# Revit family: Doorset_Porte palière blindée destinée au projet de réhabilitation BELLECOUR_ASSA ABLOY FR_Hardware 3D-05
name_source: partatom
category: Doors
revit_build: Autodesk Revit 2015 (Build: 20160512_0715(x64)
units: mm (PartAtom-declared; Revit-internal decimal feet)

## types (1)
- 914x2198 mm (900 x 2200mm)
    Architectural Hardware = 1x Ensemble béquillage SCULT_Architectural hardware_Vachette [AN. 204367 4]
    Assembly Code = B2030
    BIMobject Brand = ASSA ABLOY FR
    BIMobject Product Family = Exterior Door Solutions
    BIMobject Product Group = Security doors and fittings
    BIMobject Product Page = https://www.bimobject.com
    BIMobject Unique ref = ED-ML-MC-FR16
    Clear Width = 852 mm  [stored 2.79528 ft]
    Description = La porte anti-effraction certifiée  A2P BP1
    Edition number = 1
    Frame Height = 2200 mm
    Frame Material = Metal - Assa Abloy - Steel
    Frame Width = 900 mm  [stored 2.95276 ft]
    Function = Exterior
    Handle Height = 1100 mm
    Handle Position = 81 mm  [stored 0.265748 ft]
    Hardware Set = ED-ML-MC-FR16
    Height = 2200 mm
    IFC classification = Door
    Identity and Access Solutions = 1x Serrure 5000 SPN1 T204- D_Identity and Access Solutions_Vachette [AN. 841900 4]
    Keynote = 08100
    Lock Cases = 1x Cylindre GEMMCODE_Mechanical locks_Fichet [AN. 73960050]
    Manufacturer = ASSA ABLOY
    Maximum Door Height = 2325 mm
    Maximum Door Width = 1050 mm
    Minimum Door Height = 1952 mm  [stored 6.4042 ft]
    Minimum Door Width = 650 mm  [stored 2.13255 ft]
    Model = Doorset_Porte palière blindée destinée au projet de réhabilitation BELLECOUR_ASSA ABLOY FR_Hardware 3D
    Name = Porte palière blindée destinée au projet de réhabilitation BELLECOUR
    OmniClass Number = 23-17 11 00
    OmniClass Title = Doors
    Panel Height = 2198 mm  [stored 7.21129 ft]
    Panel Material = Metal - Assa Abloy - Steel
    Panel Width = 914 mm
    Product Guid = 56098edf-7293-468c-9a03-4614a8b7a5ac
    Provider = ASSA ABLOY FR
    Rough Height = 2210 mm  [stored 7.25066 ft]
    Rough Width = 920 mm
    Structural Opening Height = 2210 mm  [stored 7.25066 ft]
    Structural Opening Width = 920 mm
    Thickness = 62 mm  [stored 0.203412 ft]
    Type Comments = 914x2198 mm (900 x 2200mm)
    URL = https://www.fichet-serrurerie-batiment.fr
    Uniclass 1.4 Code = JL20
    Uniclass 1.4 Description = Doors
    Uniclass 2.0 Code = PR-59-23
    Uniclass 2.0 Description = Doorsets
    Wall Closure = By host
    Width = 900 mm  [stored 2.95276 ft]

note: [stored X ft] marks values corroborated as IEEE doubles in the binary element streams (Revit-internal decimal feet)

## geometry (parser evidence)
native form markers: Sweep x4
no freeform markers — native parametric forms only
